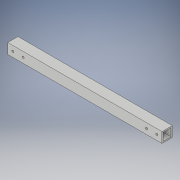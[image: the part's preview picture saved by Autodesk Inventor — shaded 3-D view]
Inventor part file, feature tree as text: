
AUTODESK INVENTOR PART (.ipt)
format: ipt  version: 2018 (Build 220112000, 112)  size: 120,832 bytes
history: native  units: in
note: dims shown in document units (in); Inventor stores cm internally (conversion verified against a paired STEP export)
features: extrude x2, sketch x2
ambient origin geometry x8: Origin, YZ Plane, XZ Plane, XY Plane, X Axis, Y Axis, Z Axis, Center Point
bodies: Solid1 (feature_tree)
feature tree (4):
  extrude  "Extrusion1"  Depth=1.0in
  extrude  "Extrusion2"  Depth=15.0in TaperAngle=0.0deg
  sketch  "Sketch1"  dims[d0=1.0in d1=1.0in]
  sketch  "Sketch2"  dims[d2=0.125in d3=15.0in d4=0.0in d5=0.5in d6=1.0in d7=0.5in d8=1.0in d9=0.2031in d10=0.2031in d11=0.2031in d12=0.2031in d13=17.0in d14=0.0in]
